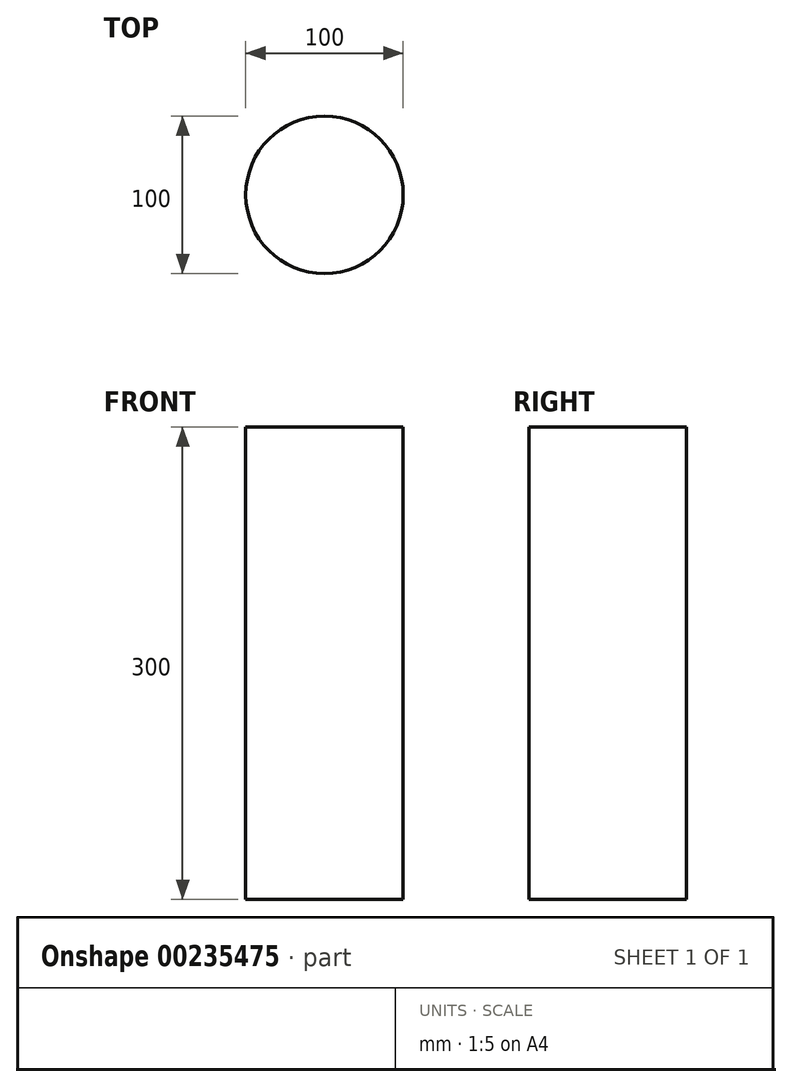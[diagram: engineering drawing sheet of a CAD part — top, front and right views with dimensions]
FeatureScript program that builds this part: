
annotation { "Feature Type Name" : "Feature", "Feature Type Description" : "" }
export const myFeature = defineFeature(function(context is Context, id is Id, definition is map)
    precondition{}
    {
        {
            var Q0;
            Q0=qCreatedBy(makeId("Top.planeOp"),FACE);
            var sketch = newSketch(context, id + "F0", { "sketchPlane" : qUnion([Q0])});
            skCircle(sketch, "E0", {"center": v(0, 0) * mm, "radius": 50 * mm});
            skSolve(sketch);
        }
        {
            var Q0;
            Q0=makeQuery(id+"F0.imprint","IMPRINT",FACE,{"disambiguationData":[TD([[makeQuery(id+"F0.imprint","IMPRINT",EDGE,{"derivedFrom":sQuery(id+"F0.wireOp",EDGE,"E0")}),1.0]])]});
            extrude(context, id + "F1", {"entities" : qUnion([Q0]), "depth" : 300 * mm});
        }
    });
